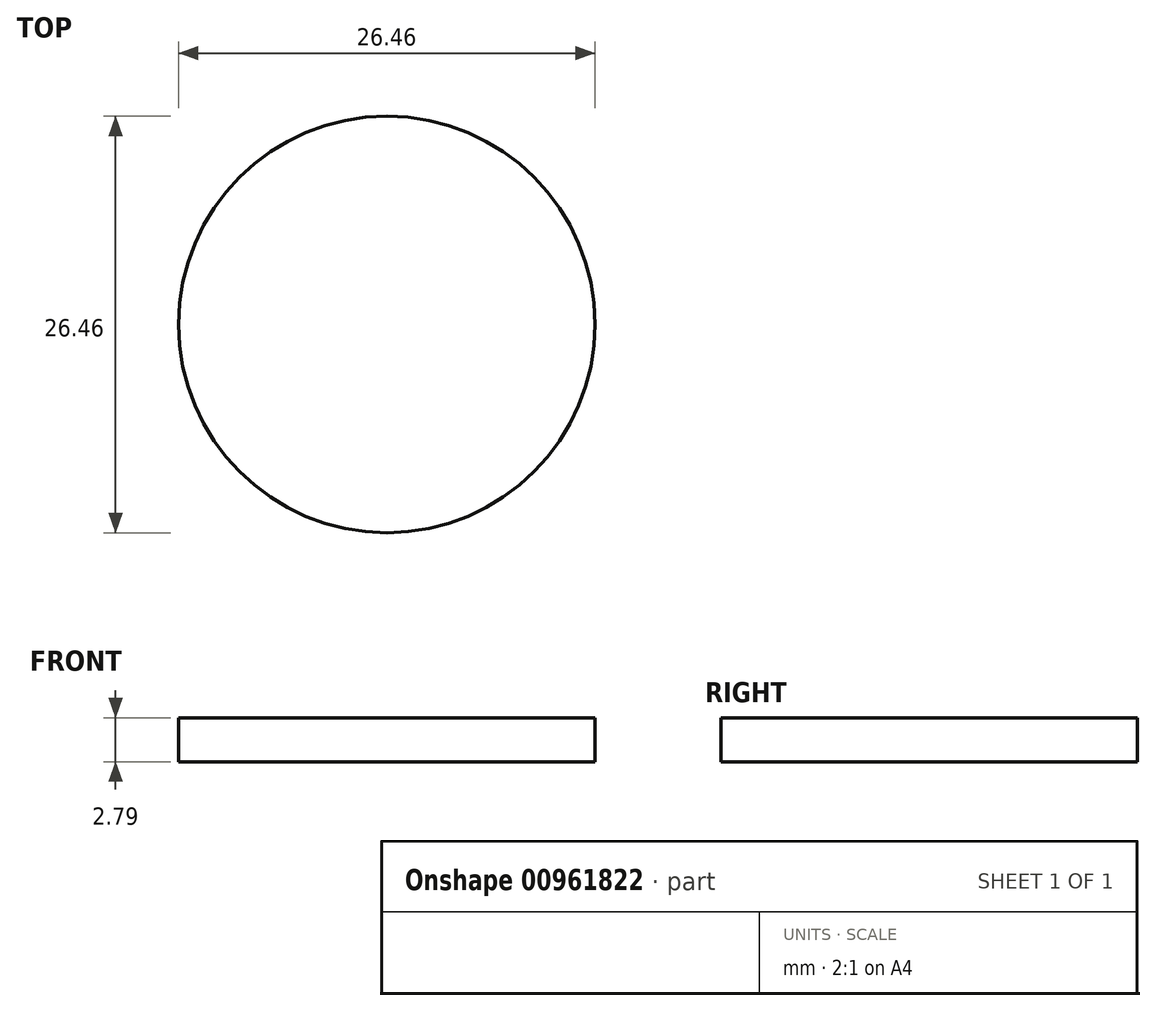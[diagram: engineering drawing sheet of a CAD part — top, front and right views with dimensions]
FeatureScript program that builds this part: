
annotation { "Feature Type Name" : "Feature", "Feature Type Description" : "" }
export const myFeature = defineFeature(function(context is Context, id is Id, definition is map)
    precondition{}
    {
        {
            var Q0;
            Q0=qCreatedBy(makeId("Top.planeOp"),FACE);
            var sketch = newSketch(context, id + "F0", { "sketchPlane" : qUnion([Q0])});
            skCircle(sketch, "E0", {"center": v(0, 0) * mm, "radius": 13.23 * mm});
            skSolve(sketch);
        }
        {
            var Q0;
            Q0 = qSketchRegion(id + "F0", true);
            extrude(context, id + "F1", {"entities" : qUnion([Q0]), "depth" : 2.8 * mm, "offsetDistance" : 25.4 * mm});
        }
    });
